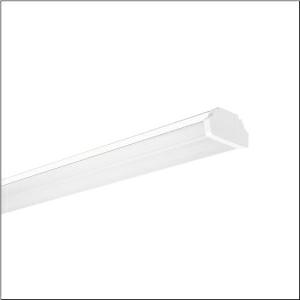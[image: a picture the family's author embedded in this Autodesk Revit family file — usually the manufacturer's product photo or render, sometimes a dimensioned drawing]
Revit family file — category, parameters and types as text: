
# Revit family: dus_31_gen_2_53bd8127v68xc2_dff7
name_source: partatom
category: Lighting Fixtures
units: mm (PartAtom-declared; Revit-internal decimal feet)

## family parameters
Cut with Voids When Loaded = No
Host = Face
Light Source = No
Part Type = Normal
Room Calculation Point = No
Round Connector Dimension = Use Diameter
Shared = No

## types (1)
- DUS 31 Gen.2 (1 x LED, 8340 lm, 47.9 W, 6500K)
    Apparent Load = 48 VA
    CIE Flux Codes = 47 80 95 93 100
    Color Rendering = 80
    Color Temperature = 6500K
    Default Elevation = 1800 mm
    Description = DUS 31 Gen.2, luminaire insert, of sheet steel, coil coated, white, length: 1.535mm, width: 81mm, height: 90mm, 5x system unit, system units: 307mm, LED rated luminous flux: 8.340lm, light colour: 865, SDCM (Standard Deviation of Colour Matching)MacAdam ≤ 3 SDCM (initial), control gear: ON/OFF, control gear: ECG, with plug, 3-pole, with phase selection, mains connection: 220..240V, AC, 50/60Hz, rated input power: 48W, through-wiring accessed according to module size, primary optical cover: cover, of PMMA, light emission: direct distribution, primary light characteristic: symmetric, protection rating (complete): IP20, protection rating (LED compartment): IP50, insulation class (complete): insulation class I (protective earthing), certification: CE, ENEC, VDE, UKCA, impact resistance: IK03, permissible ambient temperature for indoor applications: -35..+45°C, corresponds to IFS (International Featured Standards) requirements for safety and quality in the food industry, reducing of maximum allowable ambient temperature of 5°C with ceiling mounting, packaging unit: 1 piece
    Height = 95 mm
    Lamp = 1 x LED
    Lamp Light Flux = 8340 lm
    Lamp Power = 47.9 W
    Lamp count = 1
    Length = 1535 mm
    Luminous efficacy = 174 lm/W
    Manufacturer = Siteco
    ModVariant = No
    Model = 53BD8127V68XC2
    Mounting Place = Ceiling
    Mounting Type = Pendant
    Number of Poles = 1
    OnlyDefault = Yes
    Power Factor = 1
    Product Name = DUS 31 Gen.2
    Product group = luminaire insert | ceiling pendant
    ProductGroupID = 901
    Protection Class = Protection class I
    Protection Degree = IP 20
    RLX_Detail_Level = 1
    RLX_Emergency_Light_Flux = 0 lm
    RLX_Emergency_Type = 0
    RLX_Emergency_Type_DB = No
    RlxData = <blob elided: 28541 chars, md5=7bafc24e>
    Socket = socket
    Standby Power = 0 W
    System Light Flux = 8340 lm
    System Power = 48 W
    Type Comments = Product without accessories
    Type Image = l_1319596.jpg
    URL = http://relux.com
    VarID = ---
    Voltage = 0 V
    Weight = 0.00 kg
    Width = 81 mm

## geometry (parser evidence)
native form markers: Blend x4, Sweep x12
no freeform markers — native parametric forms only
